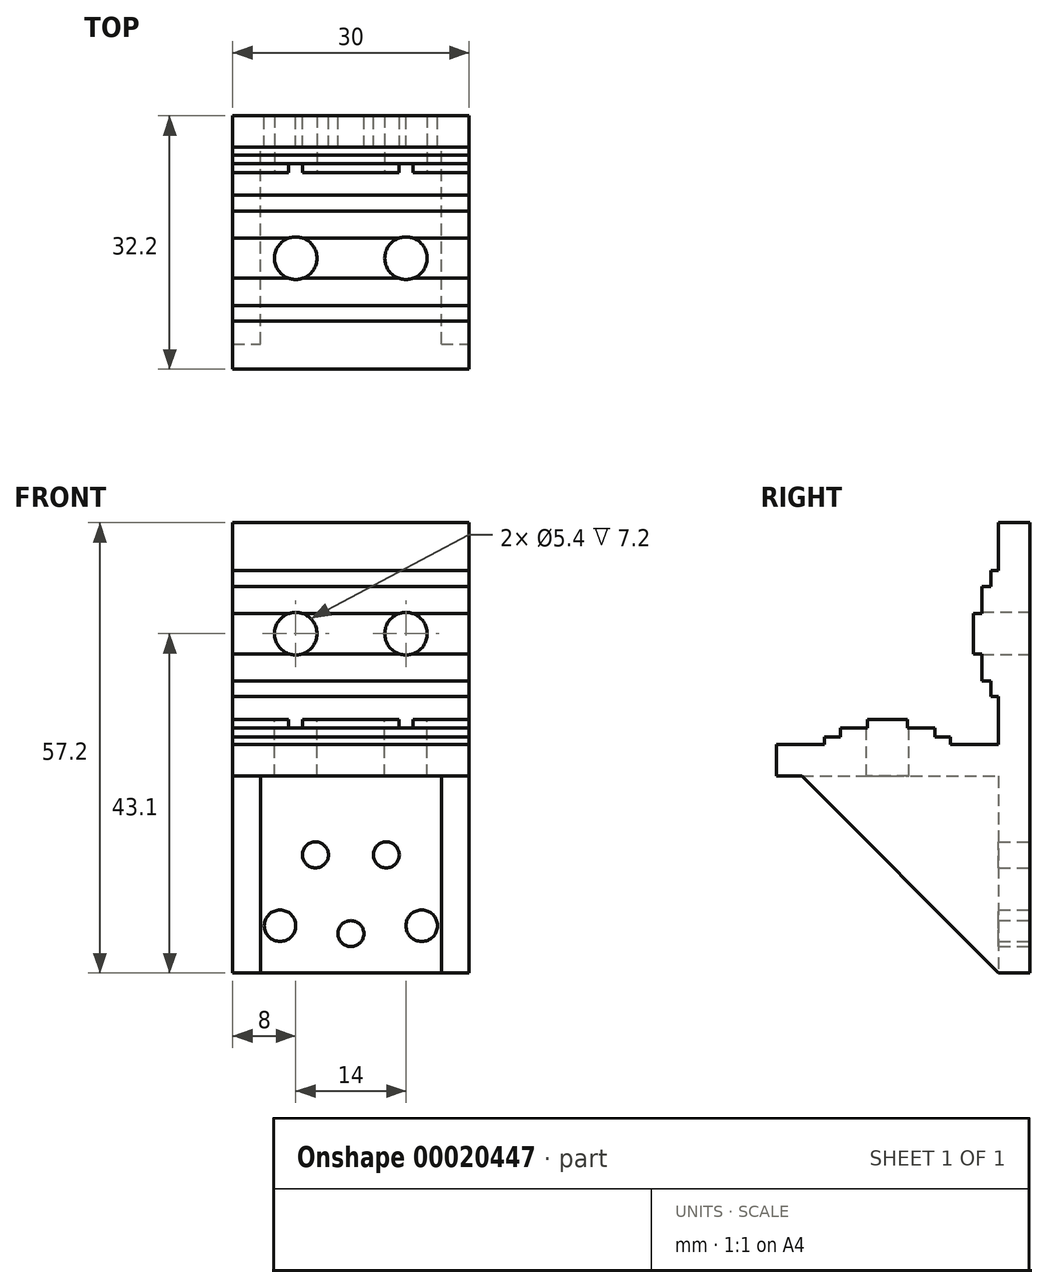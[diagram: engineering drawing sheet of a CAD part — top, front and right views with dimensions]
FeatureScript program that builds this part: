
annotation { "Feature Type Name" : "Feature", "Feature Type Description" : "" }
export const myFeature = defineFeature(function(context is Context, id is Id, definition is map)
    precondition{}
    {
        {
            var Q0;
            Q0=qCreatedBy(makeId("Front.planeOp"),FACE);
            var sketch = newSketch(context, id + "F0", { "sketchPlane" : qUnion([Q0])});
            skLineSegment(sketch, "E0", {"start": v(-15, 28.2) * mm, "end": v(-15, 0) * mm});
            skLineSegment(sketch, "E1", {"start": v(-15, 0) * mm, "end": v(-15, -4) * mm});
            skLineSegment(sketch, "E2", {"start": v(-15, -29) * mm, "end": v(15, -29) * mm});
            skLineSegment(sketch, "E3", {"start": v(15, -29) * mm, "end": v(15, -4) * mm});
            skLineSegment(sketch, "E4", {"start": v(15, 0) * mm, "end": v(15, 28.2) * mm});
            skLineSegment(sketch, "E5", {"start": v(15, 28.2) * mm, "end": v(-15, 28.2) * mm});
            skLineSegment(sketch, "E6", {"start": v(-15, 0) * mm, "end": v(0, 0) * mm, "construction": true});
            skLineSegment(sketch, "E7", {"start": v(0, 0) * mm, "end": v(15, 0) * mm, "construction": true});
            skPoint(sketch, "E8", {"position": v(0, -24) * mm});
            skPoint(sketch, "E9", {"position": v(-4.5, -14) * mm});
            skPoint(sketch, "E10", {"position": v(4.5, -14) * mm});
            skPoint(sketch, "E11", {"position": v(-9, -23) * mm});
            skPoint(sketch, "E12", {"position": v(9, -23) * mm});
            skLineSegment(sketch, "E13", {"start": v(-15, -4) * mm, "end": v(-15, -29) * mm});
            skLineSegment(sketch, "E14", {"start": v(15, -4) * mm, "end": v(15, 0) * mm});
            skLineSegment(sketch, "E15", {"start": v(-15, -4) * mm, "end": v(15, -4) * mm, "construction": true});
            skSolve(sketch);
        }
        {
            var Q0;
            Q0=makeQuery(id+"F0.imprint","IMPRINT",FACE,{"disambiguationData":[TD([[makeQuery(id+"F0.imprint","IMPRINT",EDGE,{"derivedFrom":sQuery(id+"F0.wireOp",EDGE,"E0")}),1.0]])]});
            extrude(context, id + "F1", {"entities" : qUnion([Q0]), "depth" : 4 * mm});
        }
        {
            var Q0;
            Q0=sQuery(id+"F0.wireOp",VERTEX,"E9");
            var Q1;
            Q1=sQuery(id+"F0.wireOp",VERTEX,"E10");
            var Q2;
            Q2=sQuery(id+"F0.wireOp",VERTEX,"E8");
            var Q3;
            Q3=makeQuery(id+"F1.opExtrude","SWEPT_BODY",BODY,{"disambiguationData":[OSD([sQuery(id+"F0.wireOp",EDGE,"E0"),sQuery(id+"F0.wireOp",EDGE,"E1"),sQuery(id+"F0.wireOp",EDGE,"E2"),sQuery(id+"F0.wireOp",EDGE,"E3"),sQuery(id+"F0.wireOp",EDGE,"E4"),sQuery(id+"F0.wireOp",EDGE,"E5")])]});
            hole(context, id + "F2", {"style" : HoleStyle.SIMPLE, "holeDiameter" : 3.3 * mm, "endStyle" : HoleEndStyle.THROUGH, "oppositeDirection" : true, "locations" : qUnion([Q0, Q1, Q2]), "scope" : qUnion([Q3])});
        }
        {
            var Q0;
            Q0=sQuery(id+"F0.wireOp",VERTEX,"E11");
            var Q1;
            Q1=sQuery(id+"F0.wireOp",VERTEX,"E12");
            var Q2;
            Q2=makeQuery(id+"F1.opExtrude","SWEPT_BODY",BODY,{"disambiguationData":[OSD([sQuery(id+"F0.wireOp",EDGE,"E0"),sQuery(id+"F0.wireOp",EDGE,"E1"),sQuery(id+"F0.wireOp",EDGE,"E2"),sQuery(id+"F0.wireOp",EDGE,"E3"),sQuery(id+"F0.wireOp",EDGE,"E4"),sQuery(id+"F0.wireOp",EDGE,"E5")])]});
            hole(context, id + "F3", {"style" : HoleStyle.SIMPLE, "holeDiameter" : 4 * mm, "endStyle" : HoleEndStyle.THROUGH, "oppositeDirection" : true, "locations" : qUnion([Q0, Q1]), "scope" : qUnion([Q2])});
        }
        {
            var Q0;
            Q0=makeQuery(id+"F1.opExtrude","CAP_FACE",FACE,{"disambiguationData":[OSD([sQuery(id+"F0.wireOp",EDGE,"E0"),sQuery(id+"F0.wireOp",EDGE,"E1"),sQuery(id+"F0.wireOp",EDGE,"E2"),sQuery(id+"F0.wireOp",EDGE,"E3"),sQuery(id+"F0.wireOp",EDGE,"E4"),sQuery(id+"F0.wireOp",EDGE,"E5")])],"isStart":false});
            var sketch = newSketch(context, id + "F4", { "sketchPlane" : qUnion([Q0])});
            skLineSegment(sketch, "E16", {"start": v(-15, 22.1) * mm, "end": v(-15, 6.1) * mm});
            skLineSegment(sketch, "E17", {"start": v(-15, 6.1) * mm, "end": v(15, 6.1) * mm});
            skLineSegment(sketch, "E18", {"start": v(15, 6.1) * mm, "end": v(15, 22.1) * mm});
            skLineSegment(sketch, "E19", {"start": v(15, 22.1) * mm, "end": v(-15, 22.1) * mm});
            skLineSegment(sketch, "E20", {"start": v(0, 0) * mm, "end": v(0, 6.1) * mm, "construction": true});
            skLineSegment(sketch, "E21", {"start": v(0, 22.1) * mm, "end": v(0, 28.2) * mm, "construction": true});
            skSolve(sketch);
        }
        {
            var Q0;
            Q0 = qSketchRegion(id + "F4", true);
            extrude(context, id + "F5", {"entities" : qUnion([Q0]), "operationType" : NewBodyOperationType.ADD, "depth" : 1 * mm});
        }
        {
            var Q0;
            Q0=makeQuery(id+"F5.opExtrude","CAP_FACE",FACE,{"disambiguationData":[OSD([sQuery(id+"F4.wireOp",EDGE,"E16"),sQuery(id+"F4.wireOp",EDGE,"E17"),sQuery(id+"F4.wireOp",EDGE,"E18"),sQuery(id+"F4.wireOp",EDGE,"E19")])],"isStart":false});
            var sketch = newSketch(context, id + "F6", { "sketchPlane" : qUnion([Q0])});
            skLineSegment(sketch, "E22", {"start": v(-15, 20.1) * mm, "end": v(-15, 8.1) * mm});
            skLineSegment(sketch, "E23", {"start": v(-15, 8.1) * mm, "end": v(15, 8.1) * mm});
            skLineSegment(sketch, "E24", {"start": v(15, 8.1) * mm, "end": v(15, 20.1) * mm});
            skLineSegment(sketch, "E25", {"start": v(15, 20.1) * mm, "end": v(-15, 20.1) * mm});
            skLineSegment(sketch, "E26", {"start": v(0, 6.1) * mm, "end": v(0, 8.1) * mm, "construction": true});
            skLineSegment(sketch, "E27", {"start": v(0, 20.1) * mm, "end": v(0, 22.1) * mm, "construction": true});
            skSolve(sketch);
        }
        {
            var Q0;
            Q0 = qSketchRegion(id + "F6", true);
            extrude(context, id + "F7", {"entities" : qUnion([Q0]), "operationType" : NewBodyOperationType.ADD, "depth" : 1.1 * mm});
        }
        {
            var Q0;
            Q0=makeQuery(id+"F7.opExtrude","CAP_FACE",FACE,{"disambiguationData":[OSD([sQuery(id+"F6.wireOp",EDGE,"E22"),sQuery(id+"F6.wireOp",EDGE,"E23"),sQuery(id+"F6.wireOp",EDGE,"E24"),sQuery(id+"F6.wireOp",EDGE,"E25")])],"isStart":false});
            var sketch = newSketch(context, id + "F8", { "sketchPlane" : qUnion([Q0])});
            skLineSegment(sketch, "E28", {"start": v(-15, 16.65) * mm, "end": v(-15, 11.55) * mm});
            skLineSegment(sketch, "E29", {"start": v(-15, 11.55) * mm, "end": v(15, 11.55) * mm});
            skLineSegment(sketch, "E30", {"start": v(15, 11.55) * mm, "end": v(15, 16.65) * mm});
            skLineSegment(sketch, "E31", {"start": v(15, 16.65) * mm, "end": v(-15, 16.65) * mm});
            skLineSegment(sketch, "E32", {"start": v(0, 11.55) * mm, "end": v(0, 8.1) * mm, "construction": true});
            skLineSegment(sketch, "E33", {"start": v(0, 16.65) * mm, "end": v(0, 20.1) * mm, "construction": true});
            skSolve(sketch);
        }
        {
            var Q0;
            Q0 = qSketchRegion(id + "F8", true);
            extrude(context, id + "F9", {"entities" : qUnion([Q0]), "operationType" : NewBodyOperationType.ADD, "depth" : 1.1 * mm});
        }
        {
            var Q0;
            {var subQ0=sQuery(id+"F0.wireOp",EDGE,"E0");var subQ1=sQuery(id+"F0.wireOp",EDGE,"E1");var subQ2=sQuery(id+"F0.wireOp",EDGE,"E2");var subQ3=sQuery(id+"F0.wireOp",EDGE,"E3");var subQ4=sQuery(id+"F0.wireOp",EDGE,"E4");var subQ5=sQuery(id+"F0.wireOp",EDGE,"E13");var subQ6=sQuery(id+"F0.wireOp",EDGE,"E14");Q0=makeQuery(id+"F5.boolean.opBoolean","SPLIT",FACE,{"disambiguationData":[TD([makeQuery(id+"F1.opExtrude","SWEPT_FACE",FACE,{"disambiguationData":[OSD([subQ2])]})])],"derivedFrom":makeQuery(id+"F1.opExtrude","CAP_FACE",FACE,{"disambiguationData":[OSD([subQ0,subQ1,subQ2,subQ3,subQ4,sQuery(id+"F0.wireOp",EDGE,"E5"),subQ5,subQ6])],"isStart":false})});}
            var sketch = newSketch(context, id + "F10", { "sketchPlane" : qUnion([Q0])});
            skLineSegment(sketch, "E34", {"start": v(-15, 0) * mm, "end": v(-15, -4) * mm});
            skLineSegment(sketch, "E35", {"start": v(-15, -4) * mm, "end": v(15, -4) * mm});
            skLineSegment(sketch, "E36", {"start": v(15, -4) * mm, "end": v(15, 0) * mm});
            skLineSegment(sketch, "E37", {"start": v(15, 0) * mm, "end": v(-15, 0) * mm});
            skSolve(sketch);
        }
        {
            var Q0;
            Q0 = qSketchRegion(id + "F10", true);
            extrude(context, id + "F11", {"entities" : qUnion([Q0]), "operationType" : NewBodyOperationType.ADD, "depth" : 28.2 * mm});
        }
        {
            var Q0;
            Q0=makeQuery(id+"F11.opExtrude","SWEPT_FACE",FACE,{"disambiguationData":[OSD([sQuery(id+"F10.wireOp",EDGE,"E37")])]});
            var sketch = newSketch(context, id + "F12", { "sketchPlane" : qUnion([Q0])});
            skLineSegment(sketch, "E38", {"start": v(15, -10.1) * mm, "end": v(-15, -10.1) * mm});
            skLineSegment(sketch, "E39", {"start": v(-15, -10.1) * mm, "end": v(-15, -26.1) * mm});
            skLineSegment(sketch, "E40", {"start": v(-15, -26.1) * mm, "end": v(15, -26.1) * mm});
            skLineSegment(sketch, "E41", {"start": v(15, -26.1) * mm, "end": v(15, -10.1) * mm});
            skLineSegment(sketch, "E42", {"start": v(0, -26.1) * mm, "end": v(0, -32.2) * mm, "construction": true});
            skLineSegment(sketch, "E43", {"start": v(0, -10.1) * mm, "end": v(0, -4) * mm, "construction": true});
            skSolve(sketch);
        }
        {
            var Q0;
            Q0=makeQuery(id+"F12.imprint","IMPRINT",FACE,{"disambiguationData":[TD([[makeQuery(id+"F12.imprint","IMPRINT",EDGE,{"derivedFrom":sQuery(id+"F12.wireOp",EDGE,"E38")}),1.0]])]});
            extrude(context, id + "F13", {"entities" : qUnion([Q0]), "operationType" : NewBodyOperationType.ADD, "depth" : 1 * mm});
        }
        {
            var Q0;
            Q0=makeQuery(id+"F13.opExtrude","CAP_FACE",FACE,{"disambiguationData":[OSD([sQuery(id+"F12.wireOp",EDGE,"E38"),sQuery(id+"F12.wireOp",EDGE,"E39"),sQuery(id+"F12.wireOp",EDGE,"E40"),sQuery(id+"F12.wireOp",EDGE,"E41")])],"isStart":false});
            var sketch = newSketch(context, id + "F14", { "sketchPlane" : qUnion([Q0])});
            skLineSegment(sketch, "E44.bottom", {"start": v(-15, -12.1) * mm, "end": v(15, -12.1) * mm});
            skLineSegment(sketch, "E44.top", {"start": v(-15, -24.1) * mm, "end": v(15, -24.1) * mm});
            skLineSegment(sketch, "E44.left", {"start": v(-15, -12.1) * mm, "end": v(-15, -24.1) * mm});
            skLineSegment(sketch, "E44.right", {"start": v(15, -12.1) * mm, "end": v(15, -24.1) * mm});
            skLineSegment(sketch, "E45", {"start": v(0, -12.1) * mm, "end": v(0, -10.1) * mm});
            skLineSegment(sketch, "E46", {"start": v(0, -24.1) * mm, "end": v(0, -26.1) * mm});
            skSolve(sketch);
        }
        {
            var Q0;
            {var subQ1=sQuery(id+"F14.wireOp",EDGE,"E44.left");Q0=makeQuery(id+"F14.imprint","IMPRINT",FACE,{"disambiguationData":[TD([[makeQuery(id+"F14.imprint","IMPRINT",EDGE,{"derivedFrom":subQ1}),-1.0]])]});}
            extrude(context, id + "F15", {"entities" : qUnion([Q0]), "operationType" : NewBodyOperationType.ADD, "depth" : 1.1 * mm});
        }
        {
            var Q0;
            Q0=makeQuery(id+"F15.opExtrude","CAP_FACE",FACE,{"disambiguationData":[OSD([sQuery(id+"F14.wireOp",EDGE,"E44.bottom"),sQuery(id+"F14.wireOp",EDGE,"E44.top"),sQuery(id+"F14.wireOp",EDGE,"E44.left"),sQuery(id+"F14.wireOp",EDGE,"E44.right")])],"isStart":false});
            var sketch = newSketch(context, id + "F16", { "sketchPlane" : qUnion([Q0])});
            skLineSegment(sketch, "E47.bottom", {"start": v(-15, -15.55) * mm, "end": v(15, -15.55) * mm});
            skLineSegment(sketch, "E47.top", {"start": v(-15, -20.65) * mm, "end": v(15, -20.65) * mm});
            skLineSegment(sketch, "E47.left", {"start": v(-15, -15.55) * mm, "end": v(-15, -20.65) * mm});
            skLineSegment(sketch, "E47.right", {"start": v(15, -15.55) * mm, "end": v(15, -20.65) * mm});
            skLineSegment(sketch, "E48", {"start": v(0, -15.55) * mm, "end": v(0, -12.1) * mm});
            skLineSegment(sketch, "E49", {"start": v(0, -20.65) * mm, "end": v(0, -24.1) * mm});
            skSolve(sketch);
        }
        {
            var Q0;
            {var subQ1=sQuery(id+"F16.wireOp",EDGE,"E47.left");Q0=makeQuery(id+"F16.imprint","IMPRINT",FACE,{"disambiguationData":[TD([[makeQuery(id+"F16.imprint","IMPRINT",EDGE,{"derivedFrom":subQ1}),-1.0]])]});}
            extrude(context, id + "F17", {"entities" : qUnion([Q0]), "operationType" : NewBodyOperationType.ADD, "depth" : 1.1 * mm});
        }
        {
            var Q0;
            Q0=makeQuery(id+"F9.opExtrude","CAP_FACE",FACE,{"disambiguationData":[OSD([sQuery(id+"F8.wireOp",EDGE,"E28"),sQuery(id+"F8.wireOp",EDGE,"E29"),sQuery(id+"F8.wireOp",EDGE,"E30"),sQuery(id+"F8.wireOp",EDGE,"E31")])],"isStart":false});
            var sketch = newSketch(context, id + "F18", { "sketchPlane" : qUnion([Q0])});
            skPoint(sketch, "E50", {"position": v(-7, 14.1) * mm});
            skPoint(sketch, "E51", {"position": v(7, 14.1) * mm});
            skLineSegment(sketch, "E52", {"start": v(-7, 14.1) * mm, "end": v(-7, 16.65) * mm, "construction": true});
            skLineSegment(sketch, "E53", {"start": v(-7, 14.1) * mm, "end": v(-7, 11.55) * mm, "construction": true});
            skSolve(sketch);
        }
        {
            var Q0;
            {var subQ0=sQuery(id+"F0.wireOp",EDGE,"E0");var subQ1=sQuery(id+"F0.wireOp",EDGE,"E1");var subQ2=sQuery(id+"F0.wireOp",EDGE,"E2");var subQ3=sQuery(id+"F0.wireOp",EDGE,"E3");var subQ4=sQuery(id+"F0.wireOp",EDGE,"E4");var subQ5=sQuery(id+"F0.wireOp",EDGE,"E13");var subQ6=sQuery(id+"F0.wireOp",EDGE,"E14");var subQ15=makeQuery(id+"F1.opExtrude","SWEPT_FACE",FACE,{"disambiguationData":[OSD([subQ2])]});Q0=makeQuery(id+"F11.boolean.opBoolean","SPLIT",FACE,{"disambiguationData":[TD([subQ15])],"derivedFrom":makeQuery(id+"F5.boolean.opBoolean","SPLIT",FACE,{"disambiguationData":[TD([subQ15])],"derivedFrom":makeQuery(id+"F1.opExtrude","CAP_FACE",FACE,{"disambiguationData":[OSD([subQ0,subQ1,subQ2,subQ3,subQ4,sQuery(id+"F0.wireOp",EDGE,"E5"),subQ5,subQ6])],"isStart":false})})});}
            var sketch = newSketch(context, id + "F19", { "sketchPlane" : qUnion([Q0])});
            skLineSegment(sketch, "E54.bottom", {"start": v(-15, -4) * mm, "end": v(-11.5, -4) * mm});
            skLineSegment(sketch, "E54.top", {"start": v(-15, -29) * mm, "end": v(-11.5, -29) * mm});
            skLineSegment(sketch, "E54.left", {"start": v(-15, -4) * mm, "end": v(-15, -29) * mm});
            skLineSegment(sketch, "E54.right", {"start": v(-11.5, -4) * mm, "end": v(-11.5, -29) * mm});
            skLineSegment(sketch, "E55.bottom", {"start": v(15, -4) * mm, "end": v(11.5, -4) * mm});
            skLineSegment(sketch, "E55.top", {"start": v(15, -29) * mm, "end": v(11.5, -29) * mm});
            skLineSegment(sketch, "E55.left", {"start": v(15, -4) * mm, "end": v(15, -29) * mm});
            skLineSegment(sketch, "E55.right", {"start": v(11.5, -4) * mm, "end": v(11.5, -29) * mm});
            skSolve(sketch);
        }
        {
            var Q0;
            Q0 = qSketchRegion(id + "F19", true);
            extrude(context, id + "F20", {"entities" : qUnion([Q0]), "operationType" : NewBodyOperationType.ADD, "depth" : 28 * mm});
        }
        {
            var Q0;
            Q0=makeQuery(id+"F17.opExtrude","CAP_FACE",FACE,{"disambiguationData":[OSD([sQuery(id+"F16.wireOp",EDGE,"E47.bottom"),sQuery(id+"F16.wireOp",EDGE,"E47.top"),sQuery(id+"F16.wireOp",EDGE,"E47.left"),sQuery(id+"F16.wireOp",EDGE,"E47.right")])],"isStart":false});
            var sketch = newSketch(context, id + "F21", { "sketchPlane" : qUnion([Q0])});
            skPoint(sketch, "E56", {"position": v(-7, -18.1) * mm});
            skPoint(sketch, "E57", {"position": v(7, -18.1) * mm});
            skLineSegment(sketch, "E58", {"start": v(-7, -18.1) * mm, "end": v(-7, -15.55) * mm, "construction": true});
            skLineSegment(sketch, "E59", {"start": v(-7, -18.1) * mm, "end": v(-7, -20.65) * mm, "construction": true});
            skSolve(sketch);
        }
        {
            var Q0;
            Q0=makeQuery(id+"F20.opExtrude","CAP_EDGE",EDGE,{"disambiguationData":[OSD([sQuery(id+"F19.wireOp",EDGE,"E54.top")])],"isStart":false});
            var Q1;
            Q1=makeQuery(id+"F20.opExtrude","CAP_EDGE",EDGE,{"disambiguationData":[OSD([sQuery(id+"F19.wireOp",EDGE,"E55.top")])],"isStart":false});
            chamfer(context, id + "F22", {"entities" : qUnion([Q0, Q1]), "chamferType" : ChamferType.TWO_OFFSETS, "width1" : 28 * mm, "oppositeDirection" : false, "width2" : 28 * mm, "tangentPropagation" : true});
        }
        {
            var Q0;
            Q0=sQuery(id+"F21.wireOp",VERTEX,"E56");
            var Q1;
            Q1=sQuery(id+"F21.wireOp",VERTEX,"E57");
            var Q2;
            Q2=makeQuery(id+"F1.opExtrude","SWEPT_BODY",BODY,{"disambiguationData":[OSD([sQuery(id+"F0.wireOp",EDGE,"E0"),sQuery(id+"F0.wireOp",EDGE,"E1"),sQuery(id+"F0.wireOp",EDGE,"E2"),sQuery(id+"F0.wireOp",EDGE,"E3"),sQuery(id+"F0.wireOp",EDGE,"E4"),sQuery(id+"F0.wireOp",EDGE,"E5"),sQuery(id+"F0.wireOp",EDGE,"E13"),sQuery(id+"F0.wireOp",EDGE,"E14")])]});
            hole(context, id + "F23", {"style" : HoleStyle.SIMPLE, "holeDiameter" : 5.4 * mm, "endStyle" : HoleEndStyle.THROUGH, "locations" : qUnion([Q0, Q1]), "scope" : qUnion([Q2])});
        }
        {
            var Q0;
            Q0=sQuery(id+"F18.wireOp",VERTEX,"E50");
            var Q1;
            Q1=sQuery(id+"F18.wireOp",VERTEX,"E51");
            var Q2;
            Q2=makeQuery(id+"F1.opExtrude","SWEPT_BODY",BODY,{"disambiguationData":[OSD([sQuery(id+"F0.wireOp",EDGE,"E0"),sQuery(id+"F0.wireOp",EDGE,"E1"),sQuery(id+"F0.wireOp",EDGE,"E2"),sQuery(id+"F0.wireOp",EDGE,"E3"),sQuery(id+"F0.wireOp",EDGE,"E4"),sQuery(id+"F0.wireOp",EDGE,"E5"),sQuery(id+"F0.wireOp",EDGE,"E13"),sQuery(id+"F0.wireOp",EDGE,"E14")])]});
            hole(context, id + "F24", {"style" : HoleStyle.SIMPLE, "holeDiameter" : 5.4 * mm, "endStyle" : HoleEndStyle.THROUGH, "locations" : qUnion([Q0, Q1]), "scope" : qUnion([Q2])});
        }
    });
